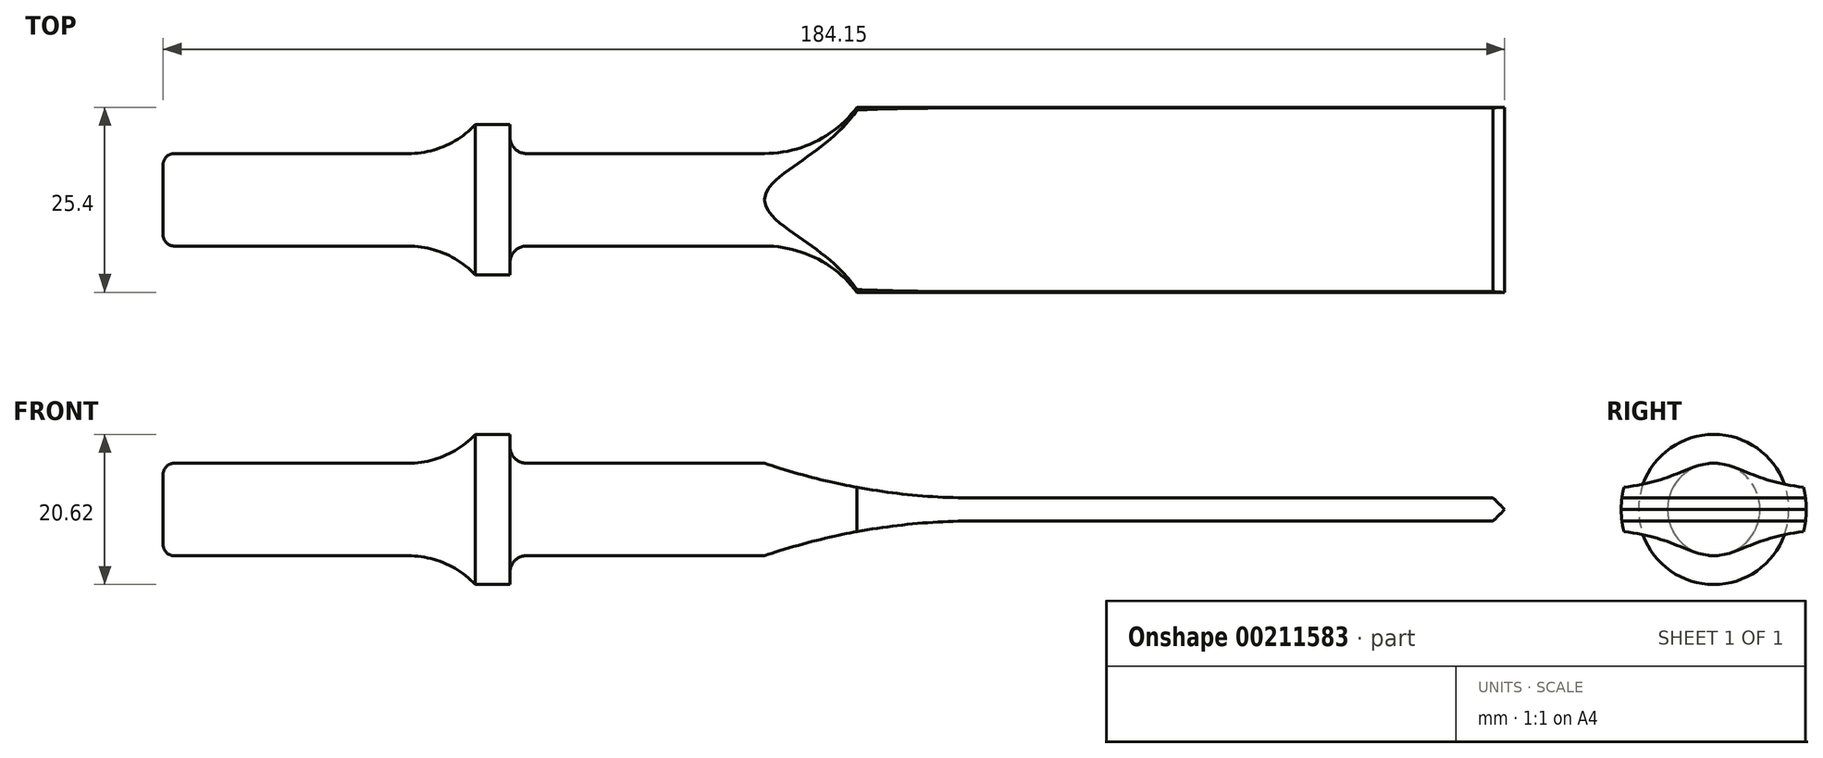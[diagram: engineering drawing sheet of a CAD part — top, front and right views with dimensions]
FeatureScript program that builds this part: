
annotation { "Feature Type Name" : "Feature", "Feature Type Description" : "" }
export const myFeature = defineFeature(function(context is Context, id is Id, definition is map)
    precondition{}
    {
        {
            var Q0;
            Q0=qCreatedBy(makeId("Front.planeOp"),FACE);
            var sketch = newSketch(context, id + "F0", { "sketchPlane" : qUnion([Q0])});
            skLineSegment(sketch, "E0", {"start": v(0, 0) * mm, "end": v(184.15, 0) * mm});
            skLineSegment(sketch, "E1", {"start": v(0, 0) * mm, "end": v(0, 4.83) * mm});
            skLineSegment(sketch, "E2", {"start": v(1.52, 6.35) * mm, "end": v(33.63, 6.35) * mm});
            skLineSegment(sketch, "E3", {"start": v(42.85, 10.31) * mm, "end": v(47.6, 10.31) * mm});
            skLineSegment(sketch, "E4", {"start": v(47.6, 10.31) * mm, "end": v(47.6, 8.64) * mm});
            skLineSegment(sketch, "E5", {"start": v(184.15, 0) * mm, "end": v(184.15, 12.7) * mm});
            skLineSegment(sketch, "E6.0", {"start": v(82.55, 0) * mm, "end": v(82.55, 12.7) * mm, "construction": true});
            skLineSegment(sketch, "E7.0", {"start": v(95.25, 0) * mm, "end": v(95.25, 12.7) * mm, "construction": true});
            skLineSegment(sketch, "E8", {"start": v(184.15, 12.7) * mm, "end": v(82.55, 12.7) * mm});
            skLineSegment(sketch, "E9.trimOffspring", {"start": v(49.89, 6.35) * mm, "end": v(82.55, 6.35) * mm});
            skArc(sketch, "E10", {"start": v(82.55, 6.35) * mm, "mid": v(89.65, 8.03) * mm, "end": v(95.25, 12.7) * mm});
            skArc(sketch, "E11", {"start": v(33.63, 6.35) * mm, "mid": v(38.65, 7.38) * mm, "end": v(42.85, 10.31) * mm});
            skPoint(sketch, "E12.visualSharp", {"position": v(0, 6.35) * mm});
            skArc(sketch, "E12.filletArc", {"start": v(1.52, 6.35) * mm, "mid": v(0.45, 5.9) * mm, "end": v(0, 4.83) * mm});
            skPoint(sketch, "E13.visualSharp", {"position": v(47.6, 6.35) * mm});
            skArc(sketch, "E13.filletArc", {"start": v(47.6, 8.64) * mm, "mid": v(48.27, 7.02) * mm, "end": v(49.89, 6.35) * mm});
            skSolve(sketch);
        }
        {
            var Q0;
            Q0=makeQuery(id+"F0.imprint","IMPRINT",FACE,{"disambiguationData":[TD([[makeQuery(id+"F0.imprint","IMPRINT",EDGE,{"derivedFrom":sQuery(id+"F0.wireOp",EDGE,"E0")}),1.0]])]});
            var Q1;
            Q1=sQuery(id+"F0.wireOp",EDGE,"E0");
            revolve(context, id + "F1", {"entities" : qUnion([Q0]), "axis" : qUnion([Q1]), "revolveType" : RevolveType.FULL});
        }
        {
            var Q0;
            Q0=qCreatedBy(makeId("Front.planeOp"),FACE);
            var sketch = newSketch(context, id + "F2", { "sketchPlane" : qUnion([Q0])});
            skLineSegment(sketch, "E14", {"start": v(0, 0) * mm, "end": v(184.15, 0) * mm, "construction": true});
            skLineSegment(sketch, "E15", {"start": v(184.15, 0) * mm, "end": v(184.15, 25.9) * mm, "construction": true});
            skLineSegment(sketch, "E16.0", {"start": v(82.55, 0) * mm, "end": v(82.55, 25.9) * mm, "construction": true});
            skLineSegment(sketch, "E17.0", {"start": v(0, 6.35) * mm, "end": v(184.15, 6.35) * mm, "construction": true});
            skPoint(sketch, "E18", {"position": v(82.55, 6.35) * mm});
            skLineSegment(sketch, "E19.0", {"start": v(111.26, 1.59) * mm, "end": v(182.56, 1.59) * mm});
            skArc(sketch, "E20", {"start": v(82.55, 6.35) * mm, "mid": v(96.7, 2.79) * mm, "end": v(111.26, 1.59) * mm});
            skLineSegment(sketch, "E21", {"start": v(184.15, 0) * mm, "end": v(182.56, 1.59) * mm});
            skLineSegment(sketch, "E22", {"start": v(82.55, 6.35) * mm, "end": v(82.55, 32.53) * mm});
            skLineSegment(sketch, "E23", {"start": v(82.55, 32.53) * mm, "end": v(191.01, 31.38) * mm});
            skLineSegment(sketch, "E24", {"start": v(191.01, 31.38) * mm, "end": v(184.15, 0) * mm});
            skLineSegment(sketch, "E25.MirrorCS", {"start": v(82.55, -6.35) * mm, "end": v(82.55, -32.53) * mm});
            skArc(sketch, "E26.MirrorCS", {"start": v(82.55, -6.35) * mm, "mid": v(96.7, -2.79) * mm, "end": v(111.26, -1.59) * mm});
            skLineSegment(sketch, "E27.MirrorCS", {"start": v(111.26, -1.59) * mm, "end": v(182.56, -1.59) * mm});
            skLineSegment(sketch, "E28.MirrorCS", {"start": v(82.55, -32.53) * mm, "end": v(191.01, -31.38) * mm});
            skLineSegment(sketch, "E29.MirrorCS", {"start": v(191.01, -31.38) * mm, "end": v(184.15, 0) * mm});
            skLineSegment(sketch, "E30.MirrorCS", {"start": v(184.15, 0) * mm, "end": v(182.56, -1.59) * mm});
            skSolve(sketch);
        }
        {
            var Q0;
            Q0=makeQuery(id+"F2.imprint","IMPRINT",FACE,{"disambiguationData":[TD([[makeQuery(id+"F2.imprint","IMPRINT",EDGE,{"derivedFrom":sQuery(id+"F2.wireOp",EDGE,"E19.0")}),1.0]])]});
            var Q1;
            Q1=makeQuery(id+"F2.imprint","IMPRINT",FACE,{"disambiguationData":[TD([[makeQuery(id+"F2.imprint","IMPRINT",EDGE,{"derivedFrom":sQuery(id+"F2.wireOp",EDGE,"E25.MirrorCS")}),1.0]])]});
            extrude(context, id + "F3", {"entities" : qUnion([Q0, Q1]), "operationType" : NewBodyOperationType.REMOVE, "oppositeDirection" : true, "depth" : 25.4 * mm});
        }
        {
            var Q0;
            Q0 = qSketchRegion(id + "F2", true);
            extrude(context, id + "F4", {"entities" : qUnion([Q0]), "operationType" : NewBodyOperationType.REMOVE, "depth" : 25.4 * mm});
        }
    });
